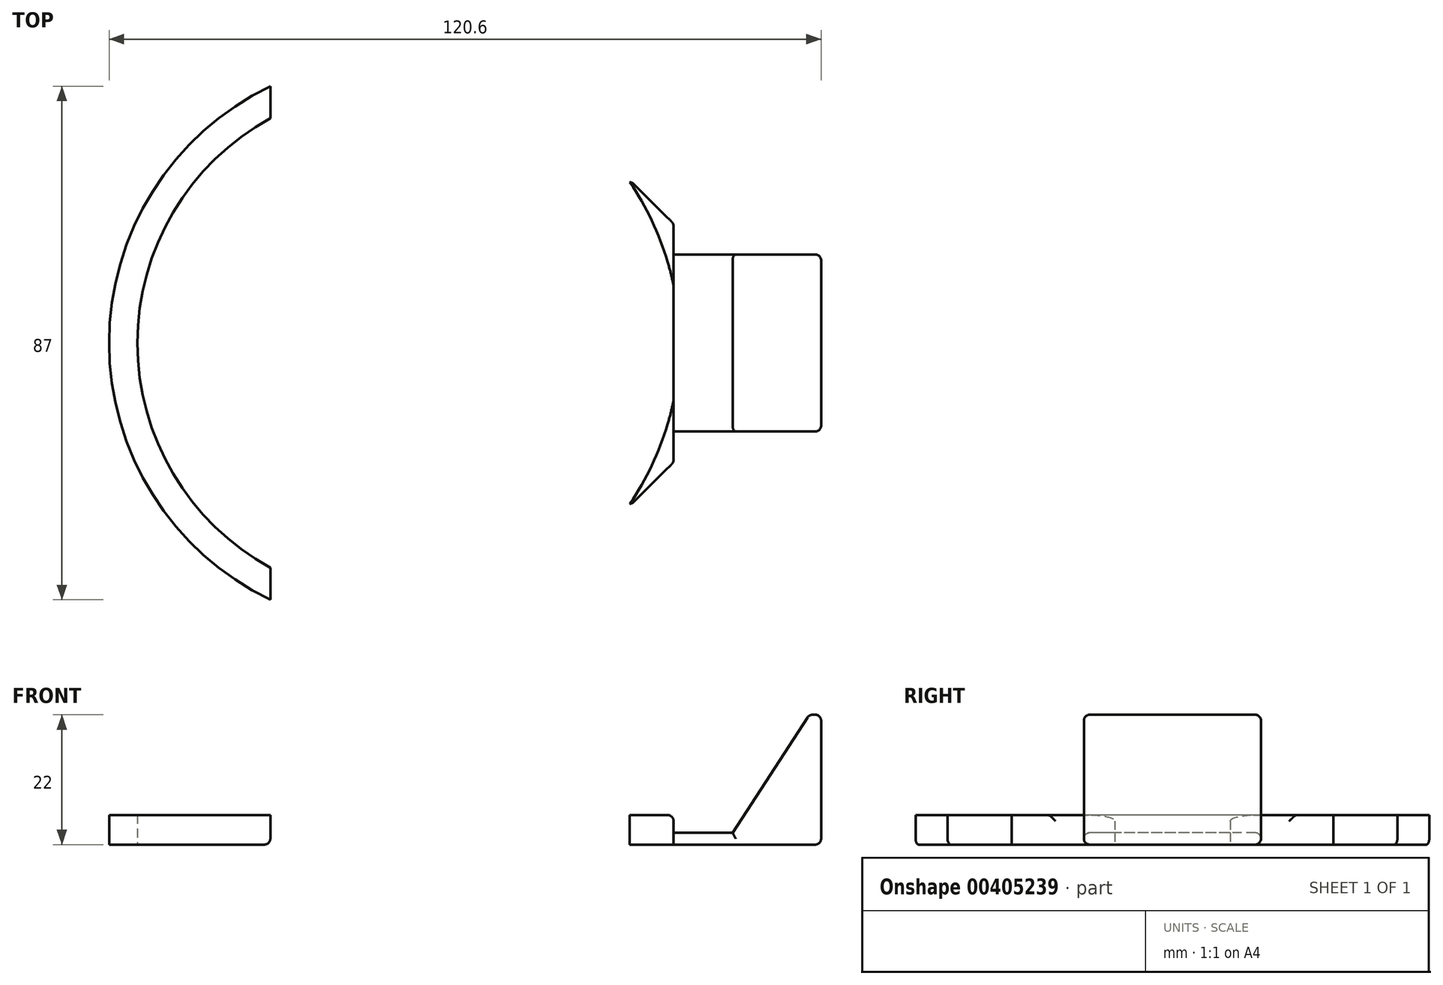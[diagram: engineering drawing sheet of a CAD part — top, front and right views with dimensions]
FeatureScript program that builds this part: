
annotation { "Feature Type Name" : "Feature", "Feature Type Description" : "" }
export const myFeature = defineFeature(function(context is Context, id is Id, definition is map)
    precondition{}
    {
        {
            var Q0;
            Q0=qCreatedBy(makeId("Top.planeOp"),FACE);
            var sketch = newSketch(context, id + "F0", { "sketchPlane" : qUnion([Q0])});
            skArc(sketch, "E0", {"start": v(0, 43.5) * mm, "mid": v(43.5, 0) * mm, "end": v(0, -43.5) * mm});
            skLineSegment(sketch, "E1", {"start": v(33.92, 27.23) * mm, "end": v(33.92, -27.23) * mm, "construction": true});
            skLineSegment(sketch, "E2", {"start": v(33.92, 27.23) * mm, "end": v(47.3, 27.23) * mm});
            skLineSegment(sketch, "E3", {"start": v(47.3, 27.23) * mm, "end": v(47.3, -27.23) * mm});
            skLineSegment(sketch, "E4", {"start": v(47.3, -27.23) * mm, "end": v(33.92, -27.23) * mm});
            skLineSegment(sketch, "E5", {"start": v(47.3, 0) * mm, "end": v(72.3, 0) * mm});
            skPoint(sketch, "E5.endSnap0", {"position": v(43.5, 0) * mm});
            skLineSegment(sketch, "E6", {"start": v(72.3, 0) * mm, "end": v(72.3, 15) * mm});
            skLineSegment(sketch, "E7", {"start": v(72.3, 15) * mm, "end": v(47.3, 15) * mm});
            skLineSegment(sketch, "E8", {"start": v(72.3, 0) * mm, "end": v(72.3, -15) * mm});
            skLineSegment(sketch, "E9", {"start": v(72.3, -15) * mm, "end": v(47.3, -15) * mm});
            skCircle(sketch, "E10", {"center": v(0, 0) * mm, "radius": 43.5 * mm});
            skCircle(sketch, "E11", {"center": v(0, 0) * mm, "radius": 48.3 * mm});
            skLineSegment(sketch, "E12", {"start": v(-21, 43.5) * mm, "end": v(-21, -43.5) * mm});
            skSolve(sketch);
        }
        {
            var Q0;
            {var subQ0=sQuery(id+"F0.wireOp",EDGE,"E2");Q0=makeQuery(id+"F0.imprint","IMPRINT",FACE,{"disambiguationData":[TD([[makeQuery(id+"F0.imprint","IMPRINT",EDGE,{"derivedFrom":subQ0}),-1.0]])]});}
            var Q1;
            {var subQ0=sQuery(id+"F0.wireOp",EDGE,"E3");var subQ1=makeQuery(id+"F0.imprint","INTERSECT",VERTEX,{"derivedFrom":[subQ0,sQuery(id+"F0.wireOp",EDGE,"E9")]});Q1=makeQuery(id+"F0.imprint","IMPRINT",FACE,{"disambiguationData":[TD([[makeQuery(id+"F0.imprint","IMPRINT",EDGE,{"disambiguationData":[TD([[subQ1,1.0]])],"derivedFrom":subQ0}),-1.0]])]});}
            var Q2;
            {var subQ0=sQuery(id+"F0.wireOp",EDGE,"E10");var subQ9=sQuery(id+"F0.wireOp",EDGE,"E2");var subQ10=makeQuery(id+"F0.imprint","INTERSECT",VERTEX,{"derivedFrom":[subQ9,subQ0]});Q2=makeQuery(id+"F0.imprint","IMPRINT",FACE,{"disambiguationData":[TD([[makeQuery(id+"F0.imprint","IMPRINT",EDGE,{"disambiguationData":[TD([[subQ10,-1.0]])],"derivedFrom":subQ9}),-1.0]])]});}
            var Q3;
            {var subQ0=sQuery(id+"F0.wireOp",EDGE,"E10");var subQ1=makeQuery(id+"F0.imprint","IMPRINT",VERTEX,{"disambiguationData":[OD(0.0)],"derivedFrom":subQ0});Q3=makeQuery(id+"F0.imprint","IMPRINT",FACE,{"disambiguationData":[TD([[makeQuery(id+"F0.imprint","IMPRINT",EDGE,{"disambiguationData":[TD([[subQ1,-1.0]])],"derivedFrom":subQ0}),-1.0]])]});}
            var Q4;
            {var subQ5=sQuery(id+"F0.wireOp",EDGE,"E10");var subQ7=makeQuery(id+"F0.imprint","IMPRINT",VERTEX,{"disambiguationData":[OD(1.0)],"derivedFrom":subQ5});Q4=makeQuery(id+"F0.imprint","IMPRINT",FACE,{"disambiguationData":[TD([[makeQuery(id+"F0.imprint","IMPRINT",EDGE,{"disambiguationData":[TD([[subQ7,1.0]])],"derivedFrom":subQ5}),-1.0]])]});}
            var Q5;
            {var subQ0=sQuery(id+"F0.wireOp",EDGE,"E12");var subQ1=sQuery(id+"F0.wireOp",EDGE,"E10");var subQ2=makeQuery(id+"F0.imprint","INTERSECT",VERTEX,{"disambiguationData":[OD(0.0)],"derivedFrom":[subQ1,subQ0]});Q5=makeQuery(id+"F0.imprint","IMPRINT",FACE,{"disambiguationData":[TD([[makeQuery(id+"F0.imprint","IMPRINT",EDGE,{"disambiguationData":[TD([[subQ2,-1.0]])],"derivedFrom":subQ1}),-1.0]])]});}
            extrude(context, id + "F1", {"entities" : qUnion([Q0, Q1, Q2, Q3, Q4, Q5]), "depth" : 5 * mm});
        }
        {
            var Q0;
            {var subQ0=sQuery(id+"F0.wireOp",EDGE,"E5");Q0=makeQuery(id+"F0.imprint","IMPRINT",FACE,{"disambiguationData":[TD([[makeQuery(id+"F0.imprint","IMPRINT",EDGE,{"derivedFrom":subQ0}),1.0]])]});}
            var Q1;
            {var subQ0=sQuery(id+"F0.wireOp",EDGE,"E5");Q1=makeQuery(id+"F0.imprint","IMPRINT",FACE,{"disambiguationData":[TD([[makeQuery(id+"F0.imprint","IMPRINT",EDGE,{"derivedFrom":subQ0}),-1.0]])]});}
            var Q2;
            {var subQ1=sQuery(id+"F0.wireOp",EDGE,"E8");Q2=makeQuery(id+"F0.imprint","IMPRINT",FACE,{"disambiguationData":[TD([[makeQuery(id+"F0.imprint","IMPRINT",EDGE,{"derivedFrom":subQ1}),-1.0]])]});}
            var Q3;
            {var subQ0=sQuery(id+"F0.wireOp",EDGE,"E6");Q3=makeQuery(id+"F0.imprint","IMPRINT",FACE,{"disambiguationData":[TD([[makeQuery(id+"F0.imprint","IMPRINT",EDGE,{"derivedFrom":subQ0}),1.0]])]});}
            extrude(context, id + "F2", {"entities" : qUnion([Q0, Q1, Q2, Q3]), "operationType" : NewBodyOperationType.ADD, "depth" : 2 * mm});
        }
        {
            var Q0;
            Q0=makeQuery(id+"F2.opExtrude","CAP_FACE",FACE,{"disambiguationData":[OSD([sQuery(id+"F0.wireOp",EDGE,"E3"),sQuery(id+"F0.wireOp",EDGE,"E6"),sQuery(id+"F0.wireOp",EDGE,"E7"),sQuery(id+"F0.wireOp",EDGE,"E8"),sQuery(id+"F0.wireOp",EDGE,"E9")])],"isStart":false});
            var sketch = newSketch(context, id + "F3", { "sketchPlane" : qUnion([Q0])});
            skLineSegment(sketch, "E13", {"start": v(72.3, -15) * mm, "end": v(72.3, 15) * mm});
            skLineSegment(sketch, "E14", {"start": v(72.3, 15) * mm, "end": v(70.3, 15) * mm});
            skLineSegment(sketch, "E15", {"start": v(70.3, 15) * mm, "end": v(70.3, -15) * mm});
            skLineSegment(sketch, "E16", {"start": v(70.3, -15) * mm, "end": v(72.3, -15) * mm});
            skSolve(sketch);
        }
        {
            var Q0;
            Q0=makeQuery(id+"F3.imprint","IMPRINT",FACE,{"disambiguationData":[TD([[makeQuery(id+"F3.imprint","IMPRINT",EDGE,{"derivedFrom":sQuery(id+"F3.wireOp",EDGE,"E13")}),1.0]])]});
            var Q1;
            Q1=makeQuery(id+"F3.imprint","IMPRINT",FACE,{"disambiguationData":[TD([[makeQuery(id+"F3.imprint","IMPRINT",EDGE,{"derivedFrom":sQuery(id+"F3.wireOp",EDGE,"E13")}),-1.0]])]});
            extrude(context, id + "F4", {"entities" : qUnion([Q0, Q1]), "operationType" : NewBodyOperationType.ADD, "depth" : 20 * mm});
        }
        {
            var Q0;
            Q0=makeQuery(id+"F1.opExtrude","SWEPT_EDGE",EDGE,{"disambiguationData":[OSD([sQuery(id+"F0.wireOp",EDGE,"E3"),sQuery(id+"F0.wireOp",EDGE,"E4")])]});
            var Q1;
            Q1=makeQuery(id+"F1.opExtrude","SWEPT_EDGE",EDGE,{"disambiguationData":[OSD([sQuery(id+"F0.wireOp",EDGE,"E2"),sQuery(id+"F0.wireOp",EDGE,"E3")])]});
            chamfer(context, id + "F5", {"entities" : qUnion([Q0, Q1]), "width" : 7 * mm, "tangentPropagation" : true});
        }
        {
            var Q0;
            Q0=makeQuery(id+"F4.boolean.opBoolean","MERGE",FACE,{"derivedFrom":[makeQuery(id+"F2.opExtrude","SWEPT_FACE",FACE,{"disambiguationData":[OSD([sQuery(id+"F0.wireOp",EDGE,"E9")])]}),makeQuery(id+"F4.opExtrude","SWEPT_FACE",FACE,{"disambiguationData":[OSD([sQuery(id+"F3.wireOp",EDGE,"E16")])]})]});
            var sketch = newSketch(context, id + "F6", { "sketchPlane" : qUnion([Q0])});
            skLineSegment(sketch, "E17", {"start": v(70.3, 2) * mm, "end": v(57.3, 2) * mm});
            skLineSegment(sketch, "E18", {"start": v(57.3, 2) * mm, "end": v(70.3, 22) * mm});
            skSolve(sketch);
        }
        {
            var Q0;
            Q0 = qSketchRegion(id + "F6", true);
            var Q1;
            Q1=makeQuery(id+"F6.imprint","IMPRINT",FACE,{"disambiguationData":[TD([[makeQuery(id+"F6.imprint","IMPRINT",EDGE,{"derivedFrom":sQuery(id+"F6.wireOp",EDGE,"E17")}),-1.0]])]});
            extrude(context, id + "F7", {"entities" : qUnion([Q0, Q1]), "operationType" : NewBodyOperationType.ADD, "oppositeDirection" : true, "depth" : 30 * mm});
        }
        {
            var Q0;
            Q0=makeQuery(id+"F7.opExtrude","CAP_EDGE",EDGE,{"disambiguationData":[OSD([sQuery(id+"F6.wireOp",EDGE,"E18")])],"isStart":true});
            var Q1;
            Q1=makeQuery(id+"F2.opExtrude","CAP_EDGE",EDGE,{"disambiguationData":[OSD([sQuery(id+"F0.wireOp",EDGE,"E9")])],"isStart":false});
            var Q2;
            Q2=makeQuery(id+"F2.opExtrude","CAP_EDGE",EDGE,{"disambiguationData":[OSD([sQuery(id+"F0.wireOp",EDGE,"E7")])],"isStart":false});
            var Q3;
            Q3=makeQuery(id+"F4.boolean.opBoolean","MERGE",EDGE,{"derivedFrom":[makeQuery(id+"F2.opExtrude","SWEPT_EDGE",EDGE,{"disambiguationData":[OSD([sQuery(id+"F0.wireOp",EDGE,"E8"),sQuery(id+"F0.wireOp",EDGE,"E9")])]}),makeQuery(id+"F4.opExtrude","SWEPT_EDGE",EDGE,{"disambiguationData":[OSD([sQuery(id+"F3.wireOp",EDGE,"E13"),sQuery(id+"F3.wireOp",EDGE,"E16")])]})]});
            var Q4;
            Q4=makeQuery(id+"F4.opExtrude","CAP_EDGE",EDGE,{"disambiguationData":[OSD([sQuery(id+"F3.wireOp",EDGE,"E16")])],"isStart":false});
            var Q5;
            {var subQ0=sQuery(id+"F3.wireOp",EDGE,"E15");Q5=makeQuery(id+"F7.boolean.opBoolean","MERGE",EDGE,{"derivedFrom":[makeQuery(id+"F4.opExtrude","CAP_EDGE",EDGE,{"disambiguationData":[OSD([subQ0])],"isStart":false}),makeQuery(id+"F7.opExtrude","SWEPT_EDGE",EDGE,{"disambiguationData":[OSD([sQuery(id+"F0.wireOp",EDGE,"E9"),subQ0,sQuery(id+"F3.wireOp",EDGE,"E16"),sQuery(id+"F6.wireOp",EDGE,"E18")])]})]});}
            var Q6;
            Q6=makeQuery(id+"F4.opExtrude","CAP_EDGE",EDGE,{"disambiguationData":[OSD([sQuery(id+"F3.wireOp",EDGE,"E13")])],"isStart":false});
            var Q7;
            Q7=makeQuery(id+"F7.opExtrude","CAP_EDGE",EDGE,{"disambiguationData":[OSD([sQuery(id+"F6.wireOp",EDGE,"E18")])],"isStart":false});
            var Q8;
            Q8=makeQuery(id+"F4.opExtrude","CAP_EDGE",EDGE,{"disambiguationData":[OSD([sQuery(id+"F3.wireOp",EDGE,"E14")])],"isStart":false});
            var Q9;
            Q9=makeQuery(id+"F4.boolean.opBoolean","MERGE",EDGE,{"derivedFrom":[makeQuery(id+"F2.opExtrude","SWEPT_EDGE",EDGE,{"disambiguationData":[OSD([sQuery(id+"F0.wireOp",EDGE,"E6"),sQuery(id+"F0.wireOp",EDGE,"E7")])]}),makeQuery(id+"F4.opExtrude","SWEPT_EDGE",EDGE,{"disambiguationData":[OSD([sQuery(id+"F3.wireOp",EDGE,"E13"),sQuery(id+"F3.wireOp",EDGE,"E14")])]})]});
            var Q10;
            Q10=makeQuery(id+"F2.opExtrude","CAP_EDGE",EDGE,{"disambiguationData":[OSD([sQuery(id+"F0.wireOp",EDGE,"E7")])],"isStart":true});
            var Q11;
            Q11=makeQuery(id+"F2.opExtrude","CAP_EDGE",EDGE,{"disambiguationData":[OSD([sQuery(id+"F0.wireOp",EDGE,"E6"),sQuery(id+"F0.wireOp",EDGE,"E8")])],"isStart":true});
            var Q12;
            Q12=makeQuery(id+"F2.opExtrude","CAP_EDGE",EDGE,{"disambiguationData":[OSD([sQuery(id+"F0.wireOp",EDGE,"E9")])],"isStart":true});
            var Q13;
            Q13=makeQuery(id+"F1.opExtrude","CAP_EDGE",EDGE,{"disambiguationData":[OSD([sQuery(id+"F0.wireOp",EDGE,"E3")])],"isStart":false});
            var Q14;
            {var subQ0=sQuery(id+"F0.wireOp",EDGE,"E3");Q14=makeQuery(id+"F5.opChamfer","BLEND_EDGE",EDGE,{"blendedFrom":[makeQuery(id+"F1.opExtrude","SWEPT_EDGE",EDGE,{"disambiguationData":[OSD([sQuery(id+"F0.wireOp",EDGE,"E2"),subQ0])]}),makeQuery(id+"F1.opExtrude","SWEPT_FACE",FACE,{"disambiguationData":[OSD([subQ0])]})],"blendedInto":[makeQuery(id+"F1.opExtrude","SWEPT_FACE",FACE,{"disambiguationData":[OSD([subQ0])]})]});}
            var Q15;
            {var subQ0=sQuery(id+"F0.wireOp",EDGE,"E3");Q15=makeQuery(id+"F5.opChamfer","BLEND_EDGE",EDGE,{"blendedFrom":[makeQuery(id+"F1.opExtrude","SWEPT_EDGE",EDGE,{"disambiguationData":[OSD([subQ0,sQuery(id+"F0.wireOp",EDGE,"E4")])]}),makeQuery(id+"F1.opExtrude","SWEPT_FACE",FACE,{"disambiguationData":[OSD([subQ0])]})],"blendedInto":[makeQuery(id+"F1.opExtrude","SWEPT_FACE",FACE,{"disambiguationData":[OSD([subQ0])]})]});}
            var Q16;
            {var subQ0=sQuery(id+"F0.wireOp",EDGE,"E2");Q16=makeQuery(id+"F5.opChamfer","BLEND_EDGE",EDGE,{"blendedFrom":[makeQuery(id+"F1.opExtrude","SWEPT_EDGE",EDGE,{"disambiguationData":[OSD([subQ0,sQuery(id+"F0.wireOp",EDGE,"E3")])]}),makeQuery(id+"F1.opExtrude","SWEPT_FACE",FACE,{"disambiguationData":[OSD([subQ0])]})],"blendedInto":[makeQuery(id+"F1.opExtrude","SWEPT_FACE",FACE,{"disambiguationData":[OSD([subQ0])]})]});}
            var Q17;
            {var subQ0=sQuery(id+"F0.wireOp",EDGE,"E4");Q17=makeQuery(id+"F5.opChamfer","BLEND_EDGE",EDGE,{"blendedFrom":[makeQuery(id+"F1.opExtrude","SWEPT_EDGE",EDGE,{"disambiguationData":[OSD([sQuery(id+"F0.wireOp",EDGE,"E3"),subQ0])]}),makeQuery(id+"F1.opExtrude","SWEPT_FACE",FACE,{"disambiguationData":[OSD([subQ0])]})],"blendedInto":[makeQuery(id+"F1.opExtrude","SWEPT_FACE",FACE,{"disambiguationData":[OSD([subQ0])]})]});}
            fillet(context, id + "F8", {"entities" : qUnion([Q0, Q1, Q2, Q3, Q4, Q5, Q6, Q7, Q8, Q9, Q10, Q11, Q12, Q13, Q14, Q15, Q16, Q17]), "radius" : 1 * mm, "tangentPropagation" : true, "allowEdgeOverflow" : false});
        }
        {
            var Q0;
            {var subQ0=sQuery(id+"F0.wireOp",EDGE,"E12");Q0=makeQuery(id+"F1.opExtrude","CAP_EDGE",EDGE,{"disambiguationData":[OSD([subQ0]),TDD([makeQuery(id+"F0.imprint","IMPRINT",EDGE,{"disambiguationData":[TD([[makeQuery(id+"F0.imprint","INTERSECT",VERTEX,{"disambiguationData":[OD(0.0)],"derivedFrom":[sQuery(id+"F0.wireOp",EDGE,"E11"),subQ0]}),-1.0]])],"derivedFrom":subQ0})])],"isStart":true});}
            var Q1;
            {var subQ0=sQuery(id+"F0.wireOp",EDGE,"E12");Q1=makeQuery(id+"F1.opExtrude","CAP_EDGE",EDGE,{"disambiguationData":[OSD([subQ0]),TDD([makeQuery(id+"F0.imprint","IMPRINT",EDGE,{"disambiguationData":[TD([[makeQuery(id+"F0.imprint","INTERSECT",VERTEX,{"disambiguationData":[OD(1.0)],"derivedFrom":[sQuery(id+"F0.wireOp",EDGE,"E11"),subQ0]}),1.0]])],"derivedFrom":subQ0})])],"isStart":true});}
            var Q2;
            {var subQ0=sQuery(id+"F0.wireOp",EDGE,"E11");Q2=makeQuery(id+"F1.opExtrude","CAP_EDGE",EDGE,{"disambiguationData":[OSD([subQ0]),TDD([makeQuery(id+"F0.imprint","IMPRINT",EDGE,{"disambiguationData":[TD([[makeQuery(id+"F0.imprint","INTERSECT",VERTEX,{"disambiguationData":[OD(0.0)],"derivedFrom":[subQ0,sQuery(id+"F0.wireOp",EDGE,"E12")]}),1.0]])],"derivedFrom":subQ0})])],"isStart":true});}
            var Q3;
            {var subQ0=sQuery(id+"F0.wireOp",EDGE,"E11");Q3=makeQuery(id+"F1.opExtrude","CAP_EDGE",EDGE,{"disambiguationData":[OSD([subQ0]),TDD([makeQuery(id+"F0.imprint","IMPRINT",EDGE,{"disambiguationData":[TD([[makeQuery(id+"F0.imprint","INTERSECT",VERTEX,{"disambiguationData":[OD(1.0)],"derivedFrom":[subQ0,sQuery(id+"F0.wireOp",EDGE,"E12")]}),-1.0]])],"derivedFrom":subQ0})])],"isStart":true});}
            fillet(context, id + "F9", {"entities" : qUnion([Q0, Q1, Q2, Q3]), "radius" : 1 * mm, "tangentPropagation" : true, "allowEdgeOverflow" : false});
        }
    });
